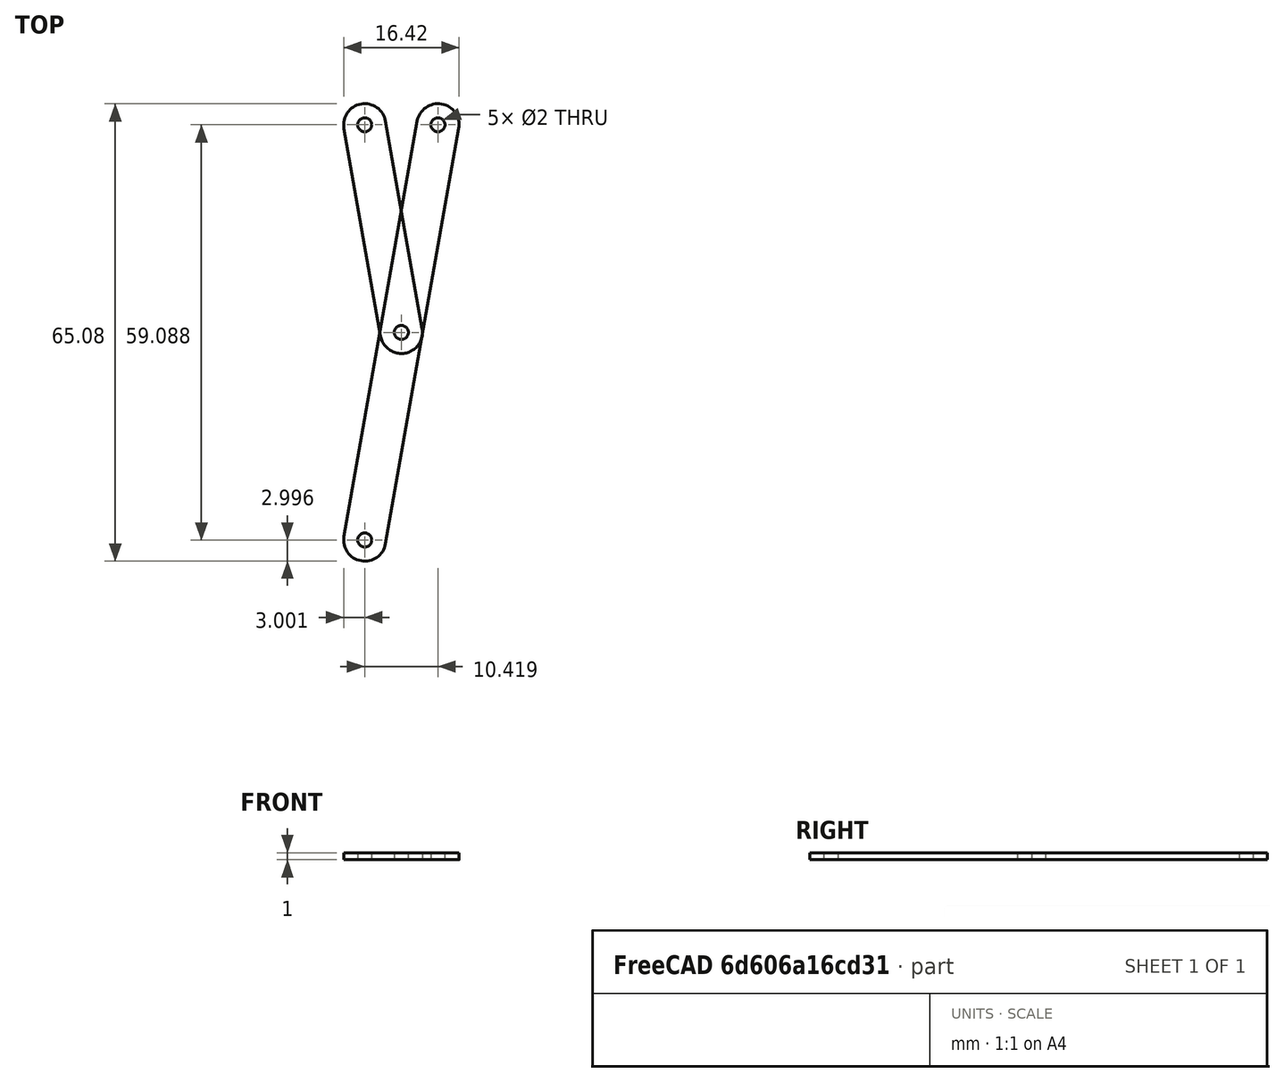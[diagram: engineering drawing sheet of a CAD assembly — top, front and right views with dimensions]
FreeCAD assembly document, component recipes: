
FREECAD ASSEMBLY — COMPONENT RECIPES ("Assambly_file_3")

This assembly document has 2 components, labeled P0..P1 below (a component is one placed body or linked part). 2 of them carry a construction recipe — the FreeCAD feature program that regenerates the part from scratch, quoted from this document or its linked companion documents; the rest are supplied as boundary geometry only. No exploded tour is included for this assembly.
COMPONENT P0 — recipe-attached ("Center_rotation_planka", modeled in this document).
Construction recipe (the document's own serialized feature program — sketch geometry with constraints, then the solid features built on it; lengths are millimeters unless a unit is written):

FEATURE [Sketcher::SketchObject] Sketch
  FullyConstrained = true
  sketch-geometry (9):
    g0: ArcOfCircle CenterX=5.20945 CenterY=29.5442 CenterZ=0 NormalX=0 NormalY=0 NormalZ=1 AngleXU=0 Radius=3 StartAngle=6.10865 EndAngle=9.25025
    g1: ArcOfCircle CenterX=-5.20945 CenterY=-29.5442 CenterZ=0 NormalX=0 NormalY=0 NormalZ=1 AngleXU=0 Radius=3 StartAngle=2.96706 EndAngle=6.10865
    g2: LineSegment StartX=2.25502 StartY=30.0652 StartZ=0 EndX=-8.16387 EndY=-29.0233 EndZ=0
    g3: LineSegment StartX=8.16387 StartY=29.0233 StartZ=0 EndX=-2.25502 EndY=-30.0652 EndZ=0
    g4: LineSegment StartX=5.20945 StartY=29.5442 StartZ=0 EndX=-5.20945 EndY=-29.5442 EndZ=0
    g5: Circle CenterX=5.20945 CenterY=29.5442 CenterZ=0 NormalX=0 NormalY=0 NormalZ=1 AngleXU=0 Radius=1
    g6: Circle CenterX=-5.20945 CenterY=-29.5442 CenterZ=0 NormalX=0 NormalY=0 NormalZ=1 AngleXU=0 Radius=5e-16
    g7: Circle CenterX=0 CenterY=0 CenterZ=0 NormalX=0 NormalY=0 NormalZ=1 AngleXU=0 Radius=1
    g8: Circle CenterX=-5.20945 CenterY=-29.5442 CenterZ=0 NormalX=0 NormalY=0 NormalZ=1 AngleXU=0 Radius=1
  constraints (19):
    c: Tangent(g0,g3) = 1.5708
    c: Tangent(g0,g2) = -1.5708
    c: Tangent(g2,g1) = -1.5708
    c: Tangent(g3,g1) = 1.5708
    c: Equal(g0,g1)
    c: Coincident(g4,g0)
    c: Coincident(g4,g1)
    c: Coincident(g5,g0)
    c: Coincident(g6,g1)
    c: Tangent(g6,g4)
    c: Coincident(g8,g1)
    c: Symmetric(g0,g1,g7)
    c: Radius(g5) = 1
    c: Equal(g5,g7)
    c: Equal(g5,g8)
    c: Distance(g4) = 60
    c: Radius(g1) = 3
    c: Coincident(g7,g-1)
    c: Angle(g-2,g4) = -0.174533
FEATURE [PartDesign::Pad] Pad
  Direction = (1,1,1)
  Length = 1
  Length2 = 100
  Profile = -> Sketch
  Type = 0
FEATURE [PartDesign::CoordinateSystem] LCS_Center_end_1
  AttacherType = Attacher::AttachEngine3D
  MapMode = 11
  Placement = pos=(5.20945,29.5442,1) rot=(0,0,1;1.5708rad)
  Support = -> [Pad]
FEATURE [PartDesign::CoordinateSystem] LCS_Center_end_2
  AttacherType = Attacher::AttachEngine3D
  MapMode = 11
  Placement = pos=(-5.20945,-29.5442,1) rot=(0,0,1;1.5708rad)
  Support = -> [Pad]
FEATURE [PartDesign::CoordinateSystem] LCS_center_center
  AttacherType = Attacher::AttachEngine3D
  MapMode = 11
  Placement = pos=(0,0,1) rot=(0,0,1;1.5708rad)
  Support = -> [Pad]
FEATURE [PartDesign::Body] Body  label="Center_rotation_planka"
  Group = -> [Sketch,Pad,LCS_Center_end_1,LCS_Center_end_2,LCS_center_center]
  Origin = -> Origin001
  Tip = -> Pad
COMPONENT P1 — recipe-attached ("Right", modeled in this document).
Construction recipe (the document's own serialized feature program — sketch geometry with constraints, then the solid features built on it; lengths are millimeters unless a unit is written):

FEATURE [Sketcher::SketchObject] Sketch001
  FullyConstrained = true
  MapMode = 5
  Support = -> [XY_Plane002]
  sketch-geometry (7):
    g0: ArcOfCircle CenterX=-5.20945 CenterY=29.5442 CenterZ=0 NormalX=0 NormalY=0 NormalZ=1 AngleXU=0 Radius=3 StartAngle=0.174533 EndAngle=3.31613
    g1: ArcOfCircle CenterX=0 CenterY=0 CenterZ=0 NormalX=0 NormalY=0 NormalZ=1 AngleXU=0 Radius=3 StartAngle=3.31613 EndAngle=6.45772
    g2: LineSegment StartX=-8.16387 StartY=29.0233 StartZ=0 EndX=-2.95442 EndY=-0.520945 EndZ=0
    g3: LineSegment StartX=-2.25502 StartY=30.0652 StartZ=0 EndX=2.95442 EndY=0.520945 EndZ=0
    g4: Circle CenterX=-5.20945 CenterY=29.5442 CenterZ=0 NormalX=0 NormalY=0 NormalZ=1 AngleXU=0 Radius=1
    g5: Circle CenterX=0 CenterY=0 CenterZ=0 NormalX=0 NormalY=0 NormalZ=1 AngleXU=0 Radius=1
    g6: LineSegment StartX=-5.20945 StartY=29.5442 StartZ=0 EndX=0 EndY=0 EndZ=0
  constraints (15):
    c: Tangent(g0,g3) = 1.5708
    c: Tangent(g0,g2) = -1.5708
    c: Tangent(g2,g1) = -1.5708
    c: Tangent(g3,g1) = 1.5708
    c: Equal(g0,g1)
    c: Coincident(g4,g0)
    c: Coincident(g5,g1)
    c: Radius(g4) = 1
    c: Radius(g5) = 1
    c: Radius(g1) = 3
    c: Coincident(g1,g-1)
    c: Coincident(g6,g0)
    c: Coincident(g6,g1)
    c: Angle(g-2,g6) = 0.174533
    c: Distance(g6) = 30
FEATURE [PartDesign::Pad] Pad001
  Direction = (1,1,1)
  Length = 1
  Length2 = 100
  Profile = -> Sketch001
  Type = 0
FEATURE [PartDesign::CoordinateSystem] LCS_right_end_2
  AttacherType = Attacher::AttachEngine3D
  MapMode = 11
  Placement = pos=(-5.20945,29.5442,1) rot=(0,0,1;1.5708rad)
  Support = -> [Pad001]
FEATURE [PartDesign::CoordinateSystem] LCS_right_end_1
  AttacherType = Attacher::AttachEngine3D
  MapMode = 11
  Placement = pos=(0,0,1) rot=(0,0,1;1.5708rad)
  Support = -> [Pad]
FEATURE [PartDesign::Body] Body001  label="Right"
  Group = -> [Sketch001,Pad001,LCS_right_end_2,LCS_right_end_1]
  Origin = -> Origin002
  Tip = -> Pad001
PROVENANCE & LICENSES
A FreeCAD (.FCStd) document from a public repository crawl; recipes are the document's own serialized feature recipes (and, for linked parts, companion documents' recipes).
License: as declared in the source repository (recorded in the dataset sidecar).
